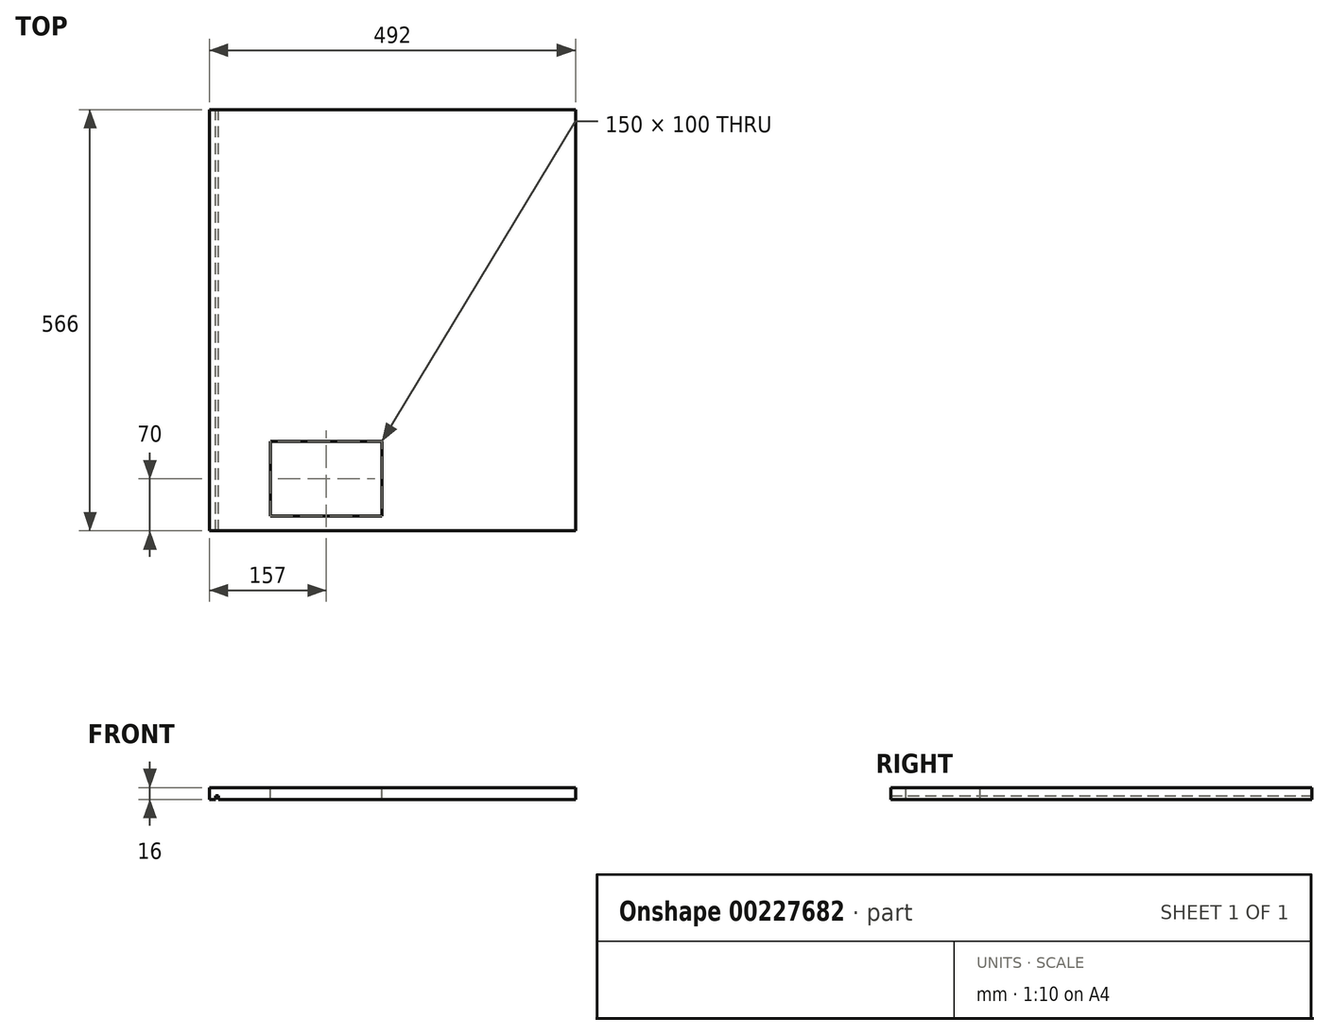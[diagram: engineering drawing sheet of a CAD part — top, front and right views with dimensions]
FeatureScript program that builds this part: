
annotation { "Feature Type Name" : "Feature", "Feature Type Description" : "" }
export const myFeature = defineFeature(function(context is Context, id is Id, definition is map)
    precondition{}
    {
        {
            var Q0;
            Q0=qCreatedBy(makeId("Top.planeOp"),FACE);
            var sketch = newSketch(context, id + "F0", { "sketchPlane" : qUnion([Q0])});
            skLineSegment(sketch, "E0.bottom", {"start": v(246, -283) * mm, "end": v(-246, -283) * mm});
            skLineSegment(sketch, "E0.top", {"start": v(246, 283) * mm, "end": v(-246, 283) * mm});
            skLineSegment(sketch, "E0.left", {"start": v(246, -283) * mm, "end": v(246, 283) * mm});
            skLineSegment(sketch, "E0.right", {"start": v(-246, -283) * mm, "end": v(-246, 283) * mm});
            skPoint(sketch, "E0.middle", {"position": v(0, 0) * mm});
            skSolve(sketch);
        }
        {
            var Q0;
            Q0=qSketchRegion(id+"F0",true);
            extrude(context, id + "F1", {"entities" : qUnion([Q0]), "depth" : 16 * mm});
        }
        {
            var Q0;
            Q0=makeQuery(id+"F1.opExtrude","CAP_FACE",FACE,{"disambiguationData":[OSD([sQuery(id+"F0.wireOp",EDGE,"E0.bottom"),sQuery(id+"F0.wireOp",EDGE,"E0.top"),sQuery(id+"F0.wireOp",EDGE,"E0.left"),sQuery(id+"F0.wireOp",EDGE,"E0.right")])],"isStart":false});
            var sketch = newSketch(context, id + "F2", { "sketchPlane" : qUnion([Q0])});
            skLineSegment(sketch, "E1.bottom", {"start": v(-164, -263) * mm, "end": v(-14, -263) * mm});
            skLineSegment(sketch, "E1.top", {"start": v(-164, -163) * mm, "end": v(-14, -163) * mm});
            skLineSegment(sketch, "E1.left", {"start": v(-164, -263) * mm, "end": v(-164, -163) * mm});
            skLineSegment(sketch, "E1.right", {"start": v(-14, -263) * mm, "end": v(-14, -163) * mm});
            skSolve(sketch);
        }
        {
            var Q0;
            Q0 = qSketchRegion(id + "F2", true);
            extrude(context, id + "F3", {"entities" : qUnion([Q0]), "operationType" : NewBodyOperationType.REMOVE, "endBound" : BoundingType.THROUGH_ALL, "oppositeDirection" : true, "depth" : 25 * mm});
        }
        {
            var Q0;
            Q0=makeQuery(id+"F1.opExtrude","SWEPT_FACE",FACE,{"disambiguationData":[OSD([sQuery(id+"F0.wireOp",EDGE,"E0.top")])]});
            var sketch = newSketch(context, id + "F4", { "sketchPlane" : qUnion([Q0])});
            skLineSegment(sketch, "E2.bottom", {"start": v(238, 0) * mm, "end": v(234, 0) * mm});
            skLineSegment(sketch, "E2.top", {"start": v(238, 5) * mm, "end": v(234, 5) * mm});
            skLineSegment(sketch, "E2.left", {"start": v(238, 0) * mm, "end": v(238, 5) * mm});
            skLineSegment(sketch, "E2.right", {"start": v(234, 0) * mm, "end": v(234, 5) * mm});
            skSolve(sketch);
        }
        {
            var Q0;
            Q0 = qSketchRegion(id + "F4", true);
            extrude(context, id + "F5", {"entities" : qUnion([Q0]), "operationType" : NewBodyOperationType.REMOVE, "endBound" : BoundingType.THROUGH_ALL, "oppositeDirection" : true, "depth" : 25 * mm});
        }
    });
